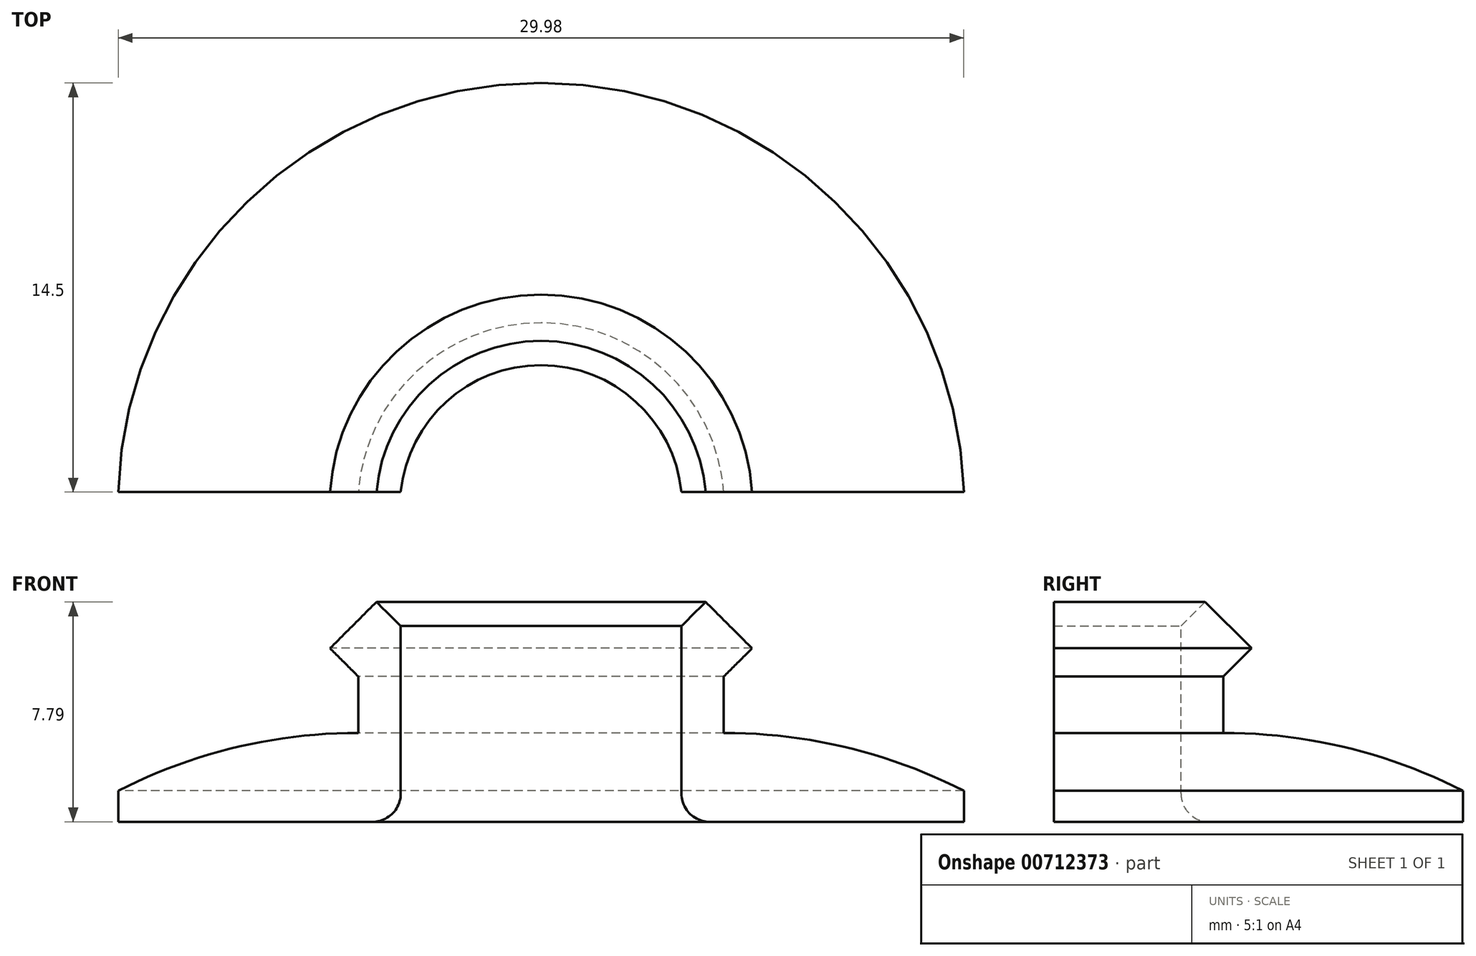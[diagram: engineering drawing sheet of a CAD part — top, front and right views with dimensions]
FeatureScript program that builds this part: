
annotation { "Feature Type Name" : "Feature", "Feature Type Description" : "" }
export const myFeature = defineFeature(function(context is Context, id is Id, definition is map)
    precondition{}
    {
        {
            var Q0;
            Q0=qCreatedBy(makeId("Front.planeOp"),FACE);
            var sketch = newSketch(context, id + "F0", { "sketchPlane" : qUnion([Q0])});
            skLineSegment(sketch, "E0", {"start": v(-5, 7.98) * mm, "end": v(-5, 2.04) * mm});
            skLineSegment(sketch, "E1", {"start": v(-5, -1.81) * mm, "end": v(-15, -1.81) * mm});
            skLineSegment(sketch, "E2", {"start": v(-15, -1.81) * mm, "end": v(-15, 2.14) * mm});
            skLineSegment(sketch, "E3", {"start": v(-6.5, 4.19) * mm, "end": v(-6.5, 6.19) * mm});
            skLineSegment(sketch, "E4", {"start": v(-6.5, 6.19) * mm, "end": v(-7.5, 7.19) * mm});
            skLineSegment(sketch, "E5", {"start": v(-7.5, 7.19) * mm, "end": v(-5.86, 8.83) * mm});
            skLineSegment(sketch, "E6", {"start": v(-5.86, 8.83) * mm, "end": v(-5, 7.98) * mm});
            skArc(sketch, "E7", {"start": v(-6.5, 4.19) * mm, "mid": v(-10.87, 3.67) * mm, "end": v(-15, 2.14) * mm});
            skLineSegment(sketch, "E8", {"start": v(-15, 1.04) * mm, "end": v(-6, 1.04) * mm});
            skArc(sketch, "E9.filletArc", {"start": v(-6, 1.04) * mm, "mid": v(-5.3, 1.33) * mm, "end": v(-5, 2.04) * mm});
            skLineSegment(sketch, "E10", {"start": v(0, 11.73) * mm, "end": v(0, -3.83) * mm});
            skSolve(sketch);
        }
        {
            var Q0;
            Q0=makeQuery(id+"F0.imprint","IMPRINT",FACE,{"disambiguationData":[TD([[makeQuery(id+"F0.imprint","IMPRINT",EDGE,{"derivedFrom":sQuery(id+"F0.wireOp",EDGE,"E0")}),-1.0]])]});
            var Q1;
            Q1=sQuery(id+"F0.wireOp",EDGE,"E10");
            revolve(context, id + "F1", {"surfaceOperationType" : NewSurfaceOperationType.NEW, "entities" : qUnion([Q0]), "axis" : qUnion([Q1]), "revolveType" : RevolveType.ONE_DIRECTION, "angle" : 180 * degree});
        }
        {
            var Q0;
            Q0=qCreatedBy(makeId("Top.planeOp"),FACE);
            var sketch = newSketch(context, id + "F2", { "sketchPlane" : qUnion([Q0])});
            skLineSegment(sketch, "E11.bottom", {"start": v(-19.24, 0.5) * mm, "end": v(18.6, 0.5) * mm});
            skLineSegment(sketch, "E11.top", {"start": v(-19.24, -0.6) * mm, "end": v(18.6, -0.6) * mm});
            skLineSegment(sketch, "E11.left", {"start": v(-19.24, 0.5) * mm, "end": v(-19.24, -0.6) * mm});
            skLineSegment(sketch, "E11.right", {"start": v(18.6, 0.5) * mm, "end": v(18.6, -0.6) * mm});
            skSolve(sketch);
        }
        {
            var Q0;
            Q0=makeQuery(id+"F2.imprint","IMPRINT",FACE,{"disambiguationData":[TD([[makeQuery(id+"F2.imprint","IMPRINT",EDGE,{"derivedFrom":sQuery(id+"F2.wireOp",EDGE,"E11.bottom")}),-1.0]])]});
            extrude(context, id + "F3", {"entities" : qUnion([Q0]), "operationType" : NewBodyOperationType.REMOVE, "depth" : 25 * mm, "offsetDistance" : 25 * mm});
        }
    });
